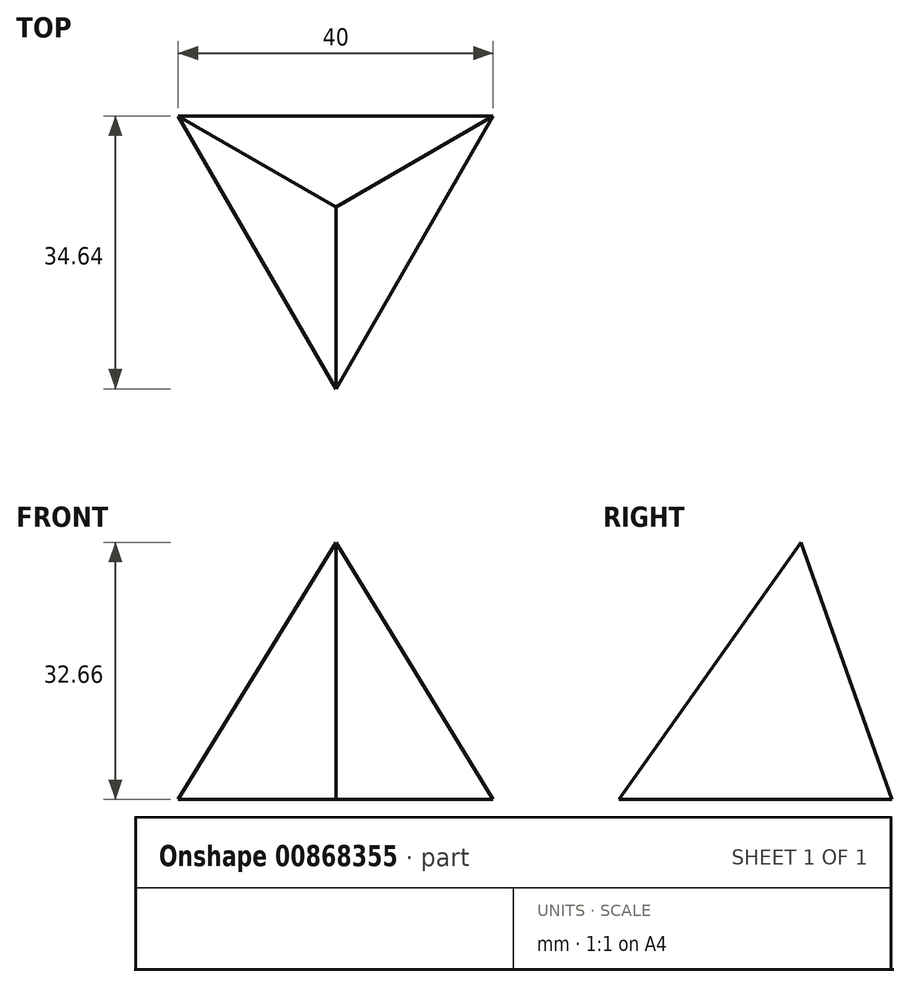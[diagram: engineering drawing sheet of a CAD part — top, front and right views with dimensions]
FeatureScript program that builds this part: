
annotation { "Feature Type Name" : "Feature", "Feature Type Description" : "" }
export const myFeature = defineFeature(function(context is Context, id is Id, definition is map)
    precondition{}
    {
        {
            var Q0;
            Q0=qCreatedBy(makeId("Top.planeOp"),FACE);
            var sketch = newSketch(context, id + "F0", { "sketchPlane" : qUnion([Q0])});
            skCircle(sketch, "E0.cCircle", {"center": v(0, 0) * mm, "radius": 11.55 * mm, "construction": true});
            skLineSegment(sketch, "E0.0", {"start": v(-20, 11.55) * mm, "end": v(20, 11.55) * mm});
            skLineSegment(sketch, "E0.1", {"start": v(20, 11.55) * mm, "end": v(0, -23.1) * mm});
            skLineSegment(sketch, "E0.2", {"start": v(0, -23.1) * mm, "end": v(-20, 11.55) * mm});
            skPoint(sketch, "E0.0.midPoint", {"position": v(0, 11.55) * mm});
            skLineSegment(sketch, "E1.MirrorCS", {"start": v(40, -23.1) * mm, "end": v(20, 11.55) * mm});
            skLineSegment(sketch, "E2.MirrorCS", {"start": v(0, -23.1) * mm, "end": v(40, -23.1) * mm});
            skLineSegment(sketch, "E3.MirrorCS", {"start": v(20, 11.55) * mm, "end": v(0, 46.19) * mm});
            skLineSegment(sketch, "E4.MirrorCS", {"start": v(0, 46.19) * mm, "end": v(-20, 11.55) * mm});
            skLineSegment(sketch, "E5.MirrorCS", {"start": v(-20, 11.55) * mm, "end": v(-40, -23.1) * mm});
            skLineSegment(sketch, "E6.MirrorCS", {"start": v(-40, -23.1) * mm, "end": v(0, -23.1) * mm});
            skSolve(sketch);
        }
        {
            var Q0;
            Q0=qCreatedBy(makeId("Front.planeOp"),FACE);
            var sketch = newSketch(context, id + "F1", { "sketchPlane" : qUnion([Q0])});
            skPoint(sketch, "E7", {"position": v(0, 32.66) * mm});
            skSolve(sketch);
        }
        {
            var Q0;
            Q0=makeQuery(id+"F0.imprint","IMPRINT",FACE,{"disambiguationData":[TD([[makeQuery(id+"F0.imprint","IMPRINT",EDGE,{"derivedFrom":sQuery(id+"F0.wireOp",EDGE,"E0.0")}),-1.0]])]});
            var Q1;
            Q1=sQuery(id+"F1.wireOp",VERTEX,"E7");
            loft(context, id + "F2", {"sheetProfilesArray" : [{ "sheetProfileEntities" : qUnion([Q0]) }, { "sheetProfileEntities" : qUnion([Q1]) }]});
        }
    });
